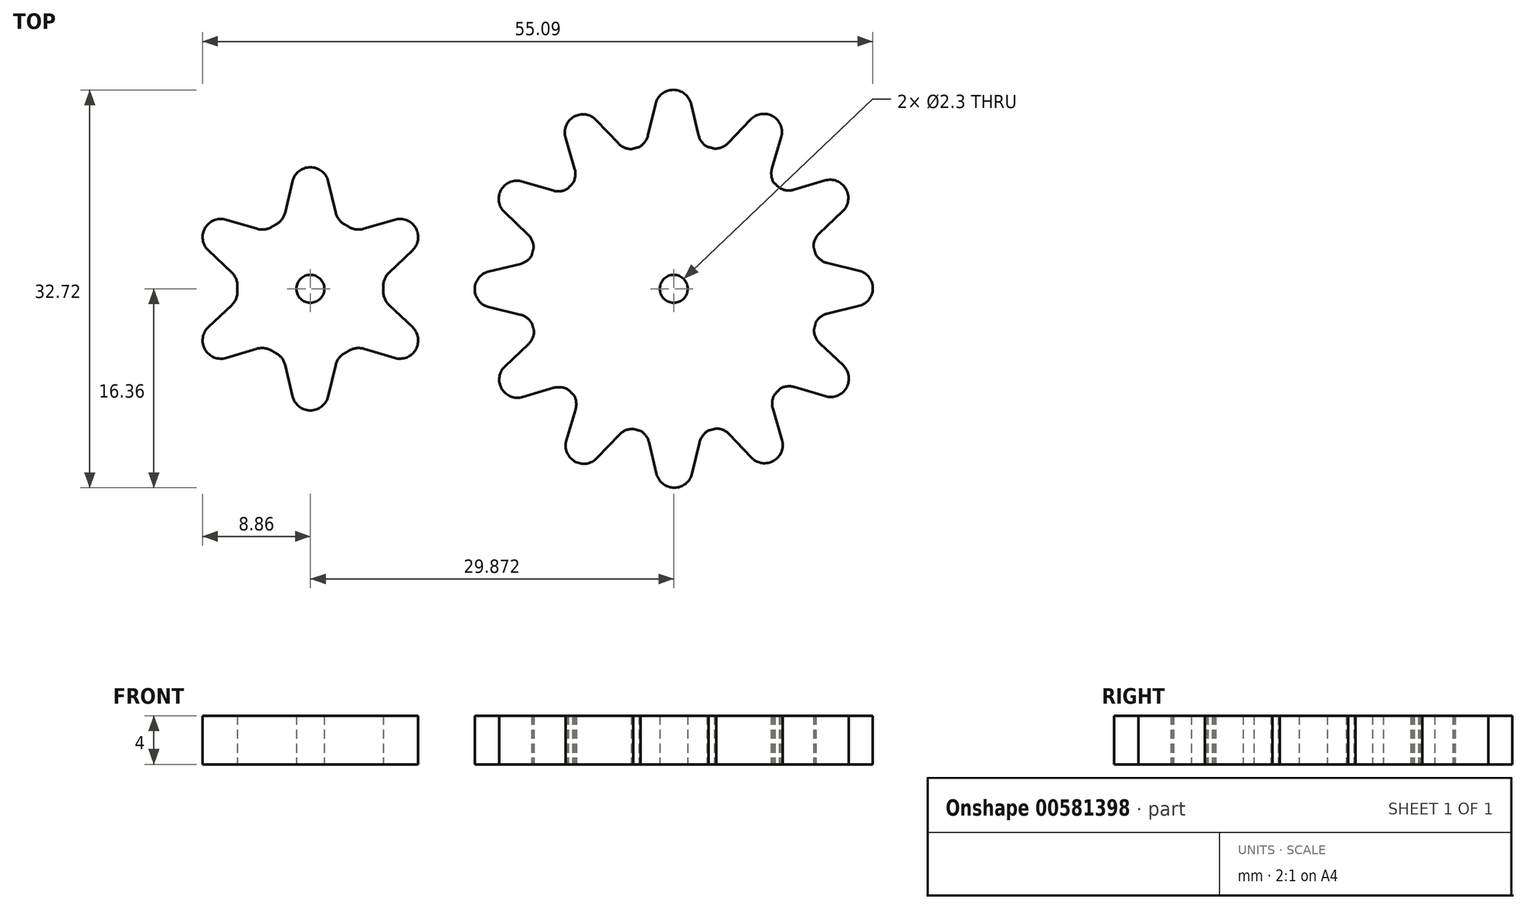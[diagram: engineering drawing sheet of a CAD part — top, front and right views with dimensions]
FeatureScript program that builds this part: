
annotation { "Feature Type Name" : "Feature", "Feature Type Description" : "" }
export const myFeature = defineFeature(function(context is Context, id is Id, definition is map)
    precondition{}
    {
        {
            var Q0;
            Q0=qCreatedBy(makeId("Top.planeOp"),FACE);
            var sketch = newSketch(context, id + "F0", { "sketchPlane" : qUnion([Q0])});
            skArc(sketch, "E0", {"start": v(-2.83, 5.3) * mm, "mid": v(-3, 5.2) * mm, "end": v(-3.17, 5.1) * mm});
            skCircle(sketch, "E1", {"center": v(0, 0) * mm, "radius": 1.15 * mm});
            skLineSegment(sketch, "E2", {"start": v(0, 0) * mm, "end": v(0, 1.15) * mm});
            skArc(sketch, "E3", {"start": v(1.46, 8.85) * mm, "mid": v(0, 10) * mm, "end": v(-1.46, 8.85) * mm});
            skLineSegment(sketch, "E4", {"start": v(-2.08, 6.26) * mm, "end": v(-1.46, 8.85) * mm});
            skLineSegment(sketch, "E5.MirrorCS", {"start": v(2.08, 6.26) * mm, "end": v(1.46, 8.85) * mm});
            skPoint(sketch, "E6.visualSharp", {"position": v(-2.25, 5.56) * mm});
            skArc(sketch, "E6.filletArc", {"start": v(-2.83, 5.3) * mm, "mid": v(-2.35, 5.7) * mm, "end": v(-2.08, 6.26) * mm});
            skPoint(sketch, "E7.visualSharp", {"position": v(2.25, 5.56) * mm});
            skArc(sketch, "E7.filletArc", {"start": v(2.08, 6.26) * mm, "mid": v(2.35, 5.7) * mm, "end": v(2.83, 5.3) * mm});
            skArc(sketch, "E8.1.0", {"start": v(-6.93, 5.69) * mm, "mid": v(-8.66, 5) * mm, "end": v(-8.4, 3.16) * mm});
            skLineSegment(sketch, "E8.1.1", {"start": v(-6.46, 1.33) * mm, "end": v(-8.4, 3.16) * mm});
            skLineSegment(sketch, "E8.1.2", {"start": v(-4.38, 4.93) * mm, "end": v(-6.93, 5.69) * mm});
            skArc(sketch, "E8.1.3", {"start": v(-6, 0.2) * mm, "mid": v(-6.1, 0.81) * mm, "end": v(-6.46, 1.33) * mm});
            skArc(sketch, "E8.1.4", {"start": v(-4.38, 4.93) * mm, "mid": v(-3.76, 4.88) * mm, "end": v(-3.17, 5.1) * mm});
            skArc(sketch, "E8.2.0", {"start": v(-8.4, -3.16) * mm, "mid": v(-8.66, -5) * mm, "end": v(-6.93, -5.69) * mm});
            skLineSegment(sketch, "E8.2.1", {"start": v(-4.38, -4.93) * mm, "end": v(-6.93, -5.69) * mm});
            skLineSegment(sketch, "E8.2.2", {"start": v(-6.46, -1.33) * mm, "end": v(-8.4, -3.16) * mm});
            skArc(sketch, "E8.2.3", {"start": v(-3.17, -5.1) * mm, "mid": v(-3.76, -4.88) * mm, "end": v(-4.38, -4.93) * mm});
            skArc(sketch, "E8.2.4", {"start": v(-6.46, -1.33) * mm, "mid": v(-6.1, -0.81) * mm, "end": v(-6, -0.2) * mm});
            skArc(sketch, "E8.3.0", {"start": v(-1.46, -8.85) * mm, "mid": v(0, -10) * mm, "end": v(1.46, -8.85) * mm});
            skLineSegment(sketch, "E8.3.1", {"start": v(2.08, -6.26) * mm, "end": v(1.46, -8.85) * mm});
            skLineSegment(sketch, "E8.3.2", {"start": v(-2.08, -6.26) * mm, "end": v(-1.46, -8.85) * mm});
            skArc(sketch, "E8.3.3", {"start": v(2.83, -5.3) * mm, "mid": v(2.35, -5.7) * mm, "end": v(2.08, -6.26) * mm});
            skArc(sketch, "E8.3.4", {"start": v(-2.08, -6.26) * mm, "mid": v(-2.35, -5.7) * mm, "end": v(-2.83, -5.3) * mm});
            skArc(sketch, "E8.4.0", {"start": v(6.93, -5.69) * mm, "mid": v(8.66, -5) * mm, "end": v(8.4, -3.16) * mm});
            skLineSegment(sketch, "E8.4.1", {"start": v(6.46, -1.33) * mm, "end": v(8.4, -3.16) * mm});
            skLineSegment(sketch, "E8.4.2", {"start": v(4.38, -4.93) * mm, "end": v(6.93, -5.69) * mm});
            skArc(sketch, "E8.4.3", {"start": v(6, -0.2) * mm, "mid": v(6.1, -0.81) * mm, "end": v(6.46, -1.33) * mm});
            skArc(sketch, "E8.4.4", {"start": v(4.38, -4.93) * mm, "mid": v(3.76, -4.88) * mm, "end": v(3.17, -5.1) * mm});
            skArc(sketch, "E8.5.0", {"start": v(8.4, 3.16) * mm, "mid": v(8.66, 5) * mm, "end": v(6.93, 5.69) * mm});
            skLineSegment(sketch, "E8.5.1", {"start": v(4.38, 4.93) * mm, "end": v(6.93, 5.69) * mm});
            skLineSegment(sketch, "E8.5.2", {"start": v(6.46, 1.33) * mm, "end": v(8.4, 3.16) * mm});
            skArc(sketch, "E8.5.3", {"start": v(3.17, 5.1) * mm, "mid": v(3.76, 4.88) * mm, "end": v(4.38, 4.93) * mm});
            skArc(sketch, "E8.5.4", {"start": v(6.46, 1.33) * mm, "mid": v(6.1, 0.81) * mm, "end": v(6, 0.2) * mm});
            skArc(sketch, "E9.trimOffspring", {"start": v(-6, 0.2) * mm, "mid": v(-6, 0) * mm, "end": v(-6, -0.2) * mm});
            skArc(sketch, "E10.trimOffspring", {"start": v(-3.17, -5.1) * mm, "mid": v(-3, -5.2) * mm, "end": v(-2.83, -5.3) * mm});
            skArc(sketch, "E11.trimOffspring", {"start": v(2.83, -5.3) * mm, "mid": v(3, -5.2) * mm, "end": v(3.17, -5.1) * mm});
            skArc(sketch, "E12.trimOffspring", {"start": v(6, -0.2) * mm, "mid": v(6, 0) * mm, "end": v(6, 0.2) * mm});
            skArc(sketch, "E13.trimOffspring", {"start": v(3.17, 5.1) * mm, "mid": v(3, 5.2) * mm, "end": v(2.83, 5.3) * mm});
            skSolve(sketch);
        }
        {
            var Q0;
            Q0=makeQuery(id+"F0.imprint","IMPRINT",FACE,{"disambiguationData":[TD([[makeQuery(id+"F0.imprint","IMPRINT",EDGE,{"derivedFrom":sQuery(id+"F0.wireOp",EDGE,"E0")}),1.0]])]});
            extrude(context, id + "F1", {"entities" : qUnion([Q0]), "depth" : 4 * mm, "offsetDistance" : 25 * mm});
        }
        {
            var Q0;
            Q0=qCreatedBy(makeId("Top.planeOp"),FACE);
            var sketch = newSketch(context, id + "F2", { "sketchPlane" : qUnion([Q0])});
            skArc(sketch, "E14.0.0", {"start": v(2.08, -6.26) * mm, "mid": v(2.35, -5.7) * mm, "end": v(2.83, -5.3) * mm});
            skArc(sketch, "E14.0.1", {"start": v(2.83, -5.3) * mm, "mid": v(3, -5.2) * mm, "end": v(3.17, -5.1) * mm});
            skArc(sketch, "E14.0.2", {"start": v(3.17, -5.1) * mm, "mid": v(3.76, -4.88) * mm, "end": v(4.38, -4.93) * mm});
            skLineSegment(sketch, "E14.0.3", {"start": v(4.38, -4.93) * mm, "end": v(6.93, -5.69) * mm});
            skArc(sketch, "E14.0.4", {"start": v(6.93, -5.69) * mm, "mid": v(8.66, -5) * mm, "end": v(8.4, -3.16) * mm});
            skLineSegment(sketch, "E14.0.5", {"start": v(8.4, -3.16) * mm, "end": v(6.46, -1.33) * mm});
            skArc(sketch, "E14.0.6", {"start": v(6.46, -1.33) * mm, "mid": v(6.1, -0.81) * mm, "end": v(6, -0.2) * mm});
            skArc(sketch, "E14.0.7", {"start": v(6, -0.2) * mm, "mid": v(6, 0) * mm, "end": v(6, 0.2) * mm});
            skArc(sketch, "E14.0.8", {"start": v(6, 0.2) * mm, "mid": v(6.1, 0.81) * mm, "end": v(6.46, 1.33) * mm});
            skLineSegment(sketch, "E14.0.9", {"start": v(6.46, 1.33) * mm, "end": v(8.4, 3.16) * mm});
            skArc(sketch, "E14.0.10", {"start": v(8.4, 3.16) * mm, "mid": v(8.66, 5) * mm, "end": v(6.93, 5.69) * mm});
            skLineSegment(sketch, "E14.0.11", {"start": v(6.93, 5.69) * mm, "end": v(4.38, 4.93) * mm});
            skArc(sketch, "E14.0.12", {"start": v(4.38, 4.93) * mm, "mid": v(3.76, 4.88) * mm, "end": v(3.17, 5.1) * mm});
            skArc(sketch, "E14.0.13", {"start": v(3.17, 5.1) * mm, "mid": v(3, 5.2) * mm, "end": v(2.83, 5.3) * mm});
            skArc(sketch, "E14.0.14", {"start": v(2.83, 5.3) * mm, "mid": v(2.35, 5.7) * mm, "end": v(2.08, 6.26) * mm});
            skLineSegment(sketch, "E14.0.15", {"start": v(2.08, 6.26) * mm, "end": v(1.46, 8.85) * mm});
            skArc(sketch, "E14.0.16", {"start": v(1.46, 8.85) * mm, "mid": v(0, 10) * mm, "end": v(-1.46, 8.85) * mm});
            skLineSegment(sketch, "E14.0.17", {"start": v(-1.46, 8.85) * mm, "end": v(-2.08, 6.26) * mm});
            skArc(sketch, "E14.0.18", {"start": v(-2.08, 6.26) * mm, "mid": v(-2.35, 5.7) * mm, "end": v(-2.83, 5.3) * mm});
            skArc(sketch, "E14.0.19", {"start": v(-2.83, 5.3) * mm, "mid": v(-3, 5.2) * mm, "end": v(-3.17, 5.1) * mm});
            skArc(sketch, "E14.0.20", {"start": v(-3.17, 5.1) * mm, "mid": v(-3.76, 4.88) * mm, "end": v(-4.38, 4.93) * mm});
            skLineSegment(sketch, "E14.0.21", {"start": v(-4.38, 4.93) * mm, "end": v(-6.93, 5.69) * mm});
            skArc(sketch, "E14.0.22", {"start": v(-6.93, 5.69) * mm, "mid": v(-8.66, 5) * mm, "end": v(-8.4, 3.16) * mm});
            skLineSegment(sketch, "E14.0.23", {"start": v(-8.4, 3.16) * mm, "end": v(-6.46, 1.33) * mm});
            skArc(sketch, "E14.0.24", {"start": v(-6.46, 1.33) * mm, "mid": v(-6.1, 0.81) * mm, "end": v(-6, 0.2) * mm});
            skArc(sketch, "E14.0.25", {"start": v(-6, 0.2) * mm, "mid": v(-6, 0) * mm, "end": v(-6, -0.2) * mm});
            skArc(sketch, "E14.0.26", {"start": v(-6, -0.2) * mm, "mid": v(-6.1, -0.81) * mm, "end": v(-6.46, -1.33) * mm});
            skLineSegment(sketch, "E14.0.27", {"start": v(-6.46, -1.33) * mm, "end": v(-8.4, -3.16) * mm});
            skArc(sketch, "E14.0.28", {"start": v(-8.4, -3.16) * mm, "mid": v(-8.66, -5) * mm, "end": v(-6.93, -5.69) * mm});
            skLineSegment(sketch, "E14.0.29", {"start": v(-6.93, -5.69) * mm, "end": v(-4.38, -4.93) * mm});
            skArc(sketch, "E14.0.30", {"start": v(-4.38, -4.93) * mm, "mid": v(-3.76, -4.88) * mm, "end": v(-3.17, -5.1) * mm});
            skArc(sketch, "E14.0.31", {"start": v(-3.17, -5.1) * mm, "mid": v(-3, -5.2) * mm, "end": v(-2.83, -5.3) * mm});
            skArc(sketch, "E14.0.32", {"start": v(-2.83, -5.3) * mm, "mid": v(-2.35, -5.7) * mm, "end": v(-2.08, -6.26) * mm});
            skLineSegment(sketch, "E14.0.33", {"start": v(-2.08, -6.26) * mm, "end": v(-1.46, -8.85) * mm});
            skArc(sketch, "E14.0.34", {"start": v(-1.46, -8.85) * mm, "mid": v(0, -10) * mm, "end": v(1.46, -8.85) * mm});
            skLineSegment(sketch, "E14.0.35", {"start": v(1.46, -8.85) * mm, "end": v(2.08, -6.26) * mm});
            skCircle(sketch, "E15.0", {"center": v(0, 0) * mm, "radius": 1.15 * mm});
            skCircle(sketch, "E16", {"center": v(29.87, 0) * mm, "radius": 1.15 * mm});
            skArc(sketch, "E17", {"start": v(27, 11.65) * mm, "mid": v(26.7, 11.57) * mm, "end": v(26.4, 11.48) * mm});
            skLineSegment(sketch, "E18", {"start": v(29.87, 0) * mm, "end": v(29.87, 1.15) * mm});
            skArc(sketch, "E19.0.14", {"start": v(32.66, 11.65) * mm, "mid": v(32.18, 12.06) * mm, "end": v(31.9, 12.62) * mm});
            skLineSegment(sketch, "E19.0.15", {"start": v(31.9, 12.62) * mm, "end": v(31.29, 15.21) * mm});
            skArc(sketch, "E19.0.16", {"start": v(31.29, 15.21) * mm, "mid": v(29.83, 16.36) * mm, "end": v(28.37, 15.21) * mm});
            skLineSegment(sketch, "E19.0.17", {"start": v(28.37, 15.21) * mm, "end": v(27.75, 12.62) * mm});
            skArc(sketch, "E19.0.18", {"start": v(27.75, 12.62) * mm, "mid": v(27.48, 12.06) * mm, "end": v(27, 11.65) * mm});
            skArc(sketch, "E20.1.0", {"start": v(23.5, 13.88) * mm, "mid": v(21.66, 14.15) * mm, "end": v(20.97, 12.42) * mm});
            skLineSegment(sketch, "E20.1.1", {"start": v(25.32, 11.95) * mm, "end": v(23.5, 13.88) * mm});
            skLineSegment(sketch, "E20.1.2", {"start": v(20.97, 12.42) * mm, "end": v(21.72, 9.87) * mm});
            skArc(sketch, "E20.1.3", {"start": v(21.72, 9.87) * mm, "mid": v(21.77, 9.25) * mm, "end": v(21.56, 8.65) * mm});
            skArc(sketch, "E20.1.4", {"start": v(26.46, 11.48) * mm, "mid": v(25.84, 11.6) * mm, "end": v(25.32, 11.95) * mm});
            skArc(sketch, "E20.2.0", {"start": v(17.4, 8.83) * mm, "mid": v(15.68, 8.14) * mm, "end": v(15.95, 6.3) * mm});
            skLineSegment(sketch, "E20.2.1", {"start": v(19.96, 8.08) * mm, "end": v(17.4, 8.83) * mm});
            skLineSegment(sketch, "E20.2.2", {"start": v(15.95, 6.3) * mm, "end": v(17.88, 4.48) * mm});
            skArc(sketch, "E20.2.3", {"start": v(17.88, 4.48) * mm, "mid": v(18.23, 3.96) * mm, "end": v(18.35, 3.34) * mm});
            skArc(sketch, "E20.2.4", {"start": v(21.18, 8.24) * mm, "mid": v(20.58, 8.03) * mm, "end": v(19.96, 8.08) * mm});
            skArc(sketch, "E20.3.0", {"start": v(14.66, 1.42) * mm, "mid": v(13.51, -0.04) * mm, "end": v(14.66, -1.5) * mm});
            skLineSegment(sketch, "E20.3.1", {"start": v(17.25, 2.04) * mm, "end": v(14.66, 1.42) * mm});
            skLineSegment(sketch, "E20.3.2", {"start": v(14.66, -1.5) * mm, "end": v(17.25, -2.12) * mm});
            skArc(sketch, "E20.3.3", {"start": v(17.25, -2.12) * mm, "mid": v(17.81, -2.4) * mm, "end": v(18.22, -2.87) * mm});
            skArc(sketch, "E20.3.4", {"start": v(18.22, 2.79) * mm, "mid": v(17.81, 2.3) * mm, "end": v(17.25, 2.04) * mm});
            skArc(sketch, "E20.4.0", {"start": v(16, -6.38) * mm, "mid": v(15.72, -8.22) * mm, "end": v(17.45, -8.9) * mm});
            skLineSegment(sketch, "E20.4.1", {"start": v(17.92, -4.55) * mm, "end": v(16, -6.38) * mm});
            skLineSegment(sketch, "E20.4.2", {"start": v(17.45, -8.9) * mm, "end": v(20, -8.15) * mm});
            skArc(sketch, "E20.4.3", {"start": v(20, -8.15) * mm, "mid": v(20.63, -8.1) * mm, "end": v(21.22, -8.31) * mm});
            skArc(sketch, "E20.4.4", {"start": v(18.39, -3.41) * mm, "mid": v(18.28, -4.03) * mm, "end": v(17.92, -4.55) * mm});
            skArc(sketch, "E20.5.0", {"start": v(21.04, -12.46) * mm, "mid": v(21.73, -14.19) * mm, "end": v(23.57, -13.92) * mm});
            skLineSegment(sketch, "E20.5.1", {"start": v(21.8, -9.91) * mm, "end": v(21.04, -12.46) * mm});
            skLineSegment(sketch, "E20.5.2", {"start": v(23.57, -13.92) * mm, "end": v(25.4, -12) * mm});
            skArc(sketch, "E20.5.3", {"start": v(25.4, -12) * mm, "mid": v(25.91, -11.64) * mm, "end": v(26.53, -11.53) * mm});
            skArc(sketch, "E20.5.4", {"start": v(21.63, -8.7) * mm, "mid": v(21.84, -9.29) * mm, "end": v(21.8, -9.91) * mm});
            skArc(sketch, "E20.6.0", {"start": v(28.45, -15.21) * mm, "mid": v(29.91, -16.36) * mm, "end": v(31.37, -15.21) * mm});
            skLineSegment(sketch, "E20.6.1", {"start": v(27.83, -12.62) * mm, "end": v(28.45, -15.21) * mm});
            skLineSegment(sketch, "E20.6.2", {"start": v(31.37, -15.21) * mm, "end": v(32, -12.62) * mm});
            skArc(sketch, "E20.6.3", {"start": v(32, -12.62) * mm, "mid": v(32.26, -12.06) * mm, "end": v(32.74, -11.65) * mm});
            skArc(sketch, "E20.6.4", {"start": v(27.08, -11.65) * mm, "mid": v(27.56, -12.06) * mm, "end": v(27.83, -12.62) * mm});
            skArc(sketch, "E20.7.0", {"start": v(36.25, -13.88) * mm, "mid": v(38.09, -14.15) * mm, "end": v(38.78, -12.42) * mm});
            skLineSegment(sketch, "E20.7.1", {"start": v(34.42, -11.95) * mm, "end": v(36.25, -13.88) * mm});
            skLineSegment(sketch, "E20.7.2", {"start": v(38.78, -12.42) * mm, "end": v(38.02, -9.87) * mm});
            skArc(sketch, "E20.7.3", {"start": v(38.02, -9.87) * mm, "mid": v(37.97, -9.25) * mm, "end": v(38.18, -8.65) * mm});
            skArc(sketch, "E20.7.4", {"start": v(33.28, -11.48) * mm, "mid": v(33.9, -11.6) * mm, "end": v(34.42, -11.95) * mm});
            skArc(sketch, "E20.8.0", {"start": v(42.34, -8.83) * mm, "mid": v(44.06, -8.14) * mm, "end": v(43.8, -6.3) * mm});
            skLineSegment(sketch, "E20.8.1", {"start": v(39.79, -8.08) * mm, "end": v(42.34, -8.83) * mm});
            skLineSegment(sketch, "E20.8.2", {"start": v(43.8, -6.3) * mm, "end": v(41.86, -4.48) * mm});
            skArc(sketch, "E20.8.3", {"start": v(41.86, -4.48) * mm, "mid": v(41.5, -3.96) * mm, "end": v(41.4, -3.34) * mm});
            skArc(sketch, "E20.8.4", {"start": v(38.57, -8.24) * mm, "mid": v(39.16, -8.03) * mm, "end": v(39.79, -8.08) * mm});
            skArc(sketch, "E20.9.0", {"start": v(45.08, -1.42) * mm, "mid": v(46.23, 0.04) * mm, "end": v(45.08, 1.5) * mm});
            skLineSegment(sketch, "E20.9.1", {"start": v(42.5, -2.04) * mm, "end": v(45.08, -1.42) * mm});
            skLineSegment(sketch, "E20.9.2", {"start": v(45.08, 1.5) * mm, "end": v(42.5, 2.12) * mm});
            skArc(sketch, "E20.9.3", {"start": v(42.5, 2.12) * mm, "mid": v(41.93, 2.4) * mm, "end": v(41.52, 2.87) * mm});
            skArc(sketch, "E20.9.4", {"start": v(41.52, -2.79) * mm, "mid": v(41.93, -2.3) * mm, "end": v(42.5, -2.04) * mm});
            skArc(sketch, "E20.10.0", {"start": v(43.75, 6.38) * mm, "mid": v(44.02, 8.22) * mm, "end": v(42.3, 8.9) * mm});
            skLineSegment(sketch, "E20.10.1", {"start": v(41.82, 4.55) * mm, "end": v(43.75, 6.38) * mm});
            skLineSegment(sketch, "E20.10.2", {"start": v(42.3, 8.9) * mm, "end": v(39.74, 8.15) * mm});
            skArc(sketch, "E20.10.3", {"start": v(39.74, 8.15) * mm, "mid": v(39.12, 8.1) * mm, "end": v(38.53, 8.31) * mm});
            skArc(sketch, "E20.10.4", {"start": v(41.36, 3.41) * mm, "mid": v(41.47, 4.03) * mm, "end": v(41.82, 4.55) * mm});
            skArc(sketch, "E20.11.0", {"start": v(38.7, 12.46) * mm, "mid": v(38.02, 14.19) * mm, "end": v(36.18, 13.92) * mm});
            skLineSegment(sketch, "E20.11.1", {"start": v(37.95, 9.91) * mm, "end": v(38.7, 12.46) * mm});
            skLineSegment(sketch, "E20.11.2", {"start": v(36.18, 13.92) * mm, "end": v(34.35, 12) * mm});
            skArc(sketch, "E20.11.3", {"start": v(34.35, 12) * mm, "mid": v(33.83, 11.64) * mm, "end": v(33.21, 11.53) * mm});
            skArc(sketch, "E20.11.4", {"start": v(38.11, 8.7) * mm, "mid": v(37.9, 9.29) * mm, "end": v(37.95, 9.91) * mm});
            skArc(sketch, "E21.trimOffspring", {"start": v(21.56, 8.65) * mm, "mid": v(21.33, 8.43) * mm, "end": v(21.12, 8.2) * mm});
            skArc(sketch, "E22.trimOffspring", {"start": v(18.35, 3.34) * mm, "mid": v(18.26, 3.03) * mm, "end": v(18.19, 2.73) * mm});
            skArc(sketch, "E23.trimOffspring", {"start": v(18.22, -2.87) * mm, "mid": v(18.3, -3.18) * mm, "end": v(18.39, -3.48) * mm});
            skArc(sketch, "E24.trimOffspring", {"start": v(21.22, -8.31) * mm, "mid": v(21.44, -8.54) * mm, "end": v(21.67, -8.76) * mm});
            skArc(sketch, "E25.trimOffspring", {"start": v(26.53, -11.53) * mm, "mid": v(26.84, -11.6) * mm, "end": v(27.14, -11.69) * mm});
            skArc(sketch, "E26.trimOffspring", {"start": v(32.74, -11.65) * mm, "mid": v(33.05, -11.57) * mm, "end": v(33.35, -11.48) * mm});
            skArc(sketch, "E27.trimOffspring", {"start": v(38.18, -8.65) * mm, "mid": v(38.4, -8.43) * mm, "end": v(38.63, -8.2) * mm});
            skArc(sketch, "E28.trimOffspring", {"start": v(41.4, -3.34) * mm, "mid": v(41.48, -3.03) * mm, "end": v(41.56, -2.73) * mm});
            skArc(sketch, "E29.trimOffspring", {"start": v(41.52, 2.87) * mm, "mid": v(41.44, 3.18) * mm, "end": v(41.36, 3.48) * mm});
            skArc(sketch, "E30.trimOffspring", {"start": v(38.53, 8.31) * mm, "mid": v(38.3, 8.54) * mm, "end": v(38.08, 8.76) * mm});
            skArc(sketch, "E31.trimOffspring", {"start": v(33.21, 11.53) * mm, "mid": v(32.9, 11.6) * mm, "end": v(32.6, 11.69) * mm});
            skSolve(sketch);
        }
        {
            var Q0;
            Q0=makeQuery(id+"F2.imprint","IMPRINT",FACE,{"disambiguationData":[TD([[makeQuery(id+"F2.imprint","IMPRINT",EDGE,{"derivedFrom":sQuery(id+"F2.wireOp",EDGE,"E16")}),-1.0]])]});
            extrude(context, id + "F3", {"entities" : qUnion([Q0]), "depth" : 4 * mm, "offsetDistance" : 25 * mm});
        }
    });
